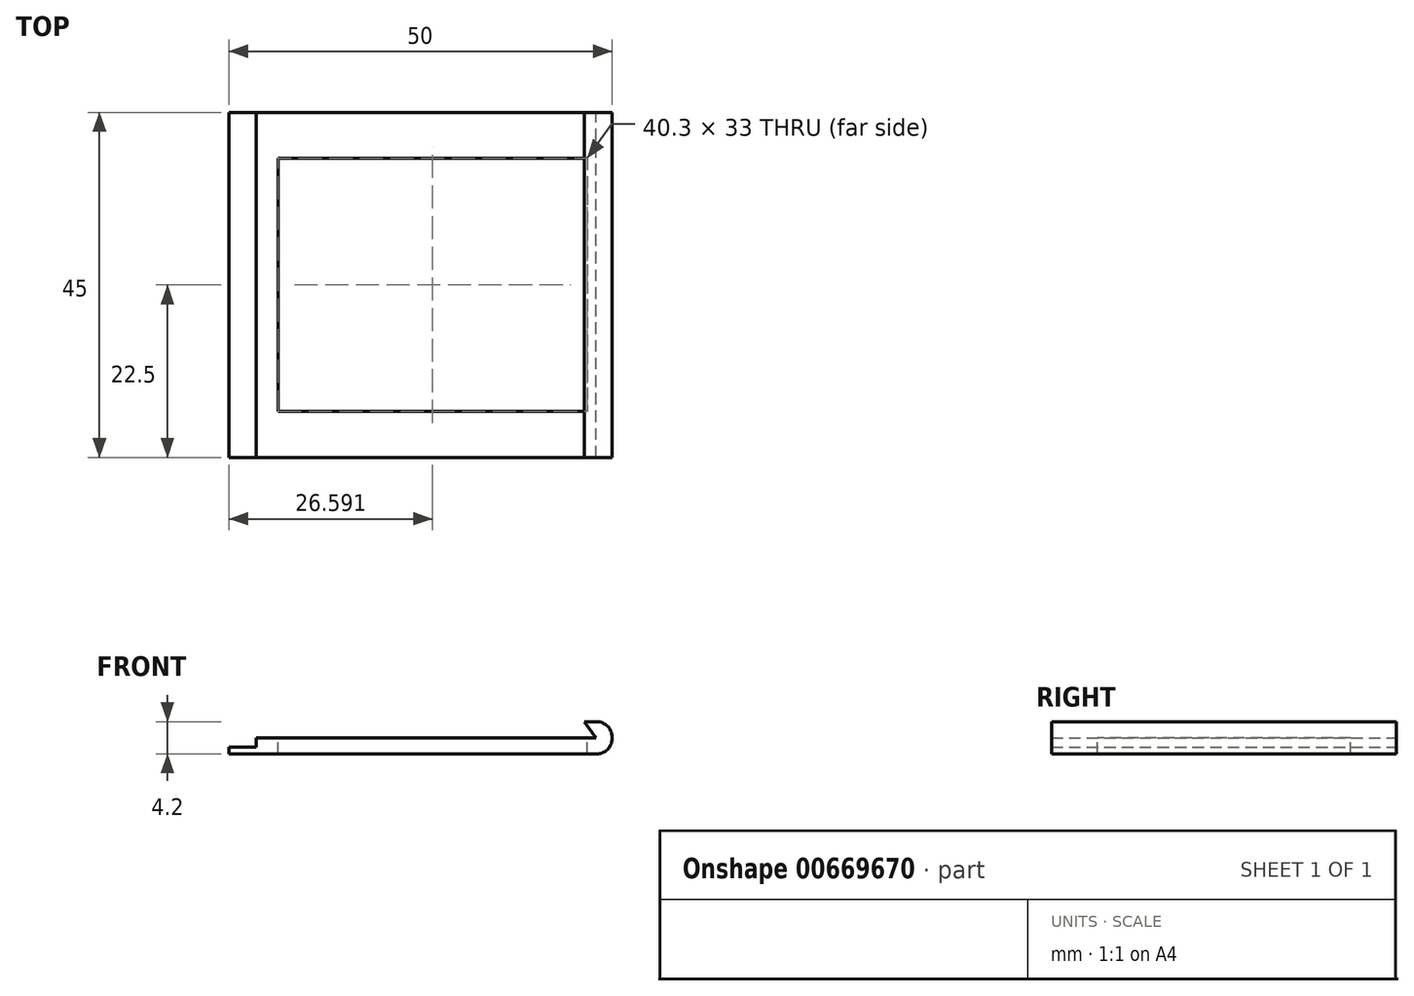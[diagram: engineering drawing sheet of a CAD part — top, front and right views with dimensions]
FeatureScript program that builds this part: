
annotation { "Feature Type Name" : "Feature", "Feature Type Description" : "" }
export const myFeature = defineFeature(function(context is Context, id is Id, definition is map)
    precondition{}
    {
        {
            var Q0;
            Q0=qCreatedBy(makeId("Front.planeOp"),FACE);
            var sketch = newSketch(context, id + "F0", { "sketchPlane" : qUnion([Q0])});
            skLineSegment(sketch, "E0", {"start": v(-9.9, 0.9) * mm, "end": v(-9.9, 0) * mm});
            skLineSegment(sketch, "E1", {"start": v(-9.9, 0) * mm, "end": v(40.1, 0) * mm});
            skLineSegment(sketch, "E2", {"start": v(40.1, 0) * mm, "end": v(40.1, 2.1) * mm});
            skLineSegment(sketch, "E3", {"start": v(40.1, 2.1) * mm, "end": v(-6.3, 2.1) * mm});
            skLineSegment(sketch, "E4", {"start": v(-6.3, 2.1) * mm, "end": v(-6.3, 0.9) * mm});
            skLineSegment(sketch, "E5", {"start": v(-6.3, 0.9) * mm, "end": v(-9.9, 0.9) * mm});
            skLineSegment(sketch, "E6", {"start": v(38, 2.1) * mm, "end": v(36.5, 4.2) * mm});
            skLineSegment(sketch, "E7", {"start": v(36.5, 4.2) * mm, "end": v(40.1, 4.2) * mm});
            skLineSegment(sketch, "E8", {"start": v(40.1, 4.2) * mm, "end": v(40.1, 2.1) * mm});
            skSolve(sketch);
        }
        {
            var Q0;
            Q0=makeQuery(id+"F0.imprint","IMPRINT",FACE,{"disambiguationData":[TD([[makeQuery(id+"F0.imprint","IMPRINT",EDGE,{"derivedFrom":sQuery(id+"F0.wireOp",EDGE,"E0")}),1.0]])]});
            var Q1;
            {var subQ2=sQuery(id+"F0.wireOp",EDGE,"E6");Q1=makeQuery(id+"F0.imprint","IMPRINT",FACE,{"disambiguationData":[TD([[makeQuery(id+"F0.imprint","IMPRINT",EDGE,{"derivedFrom":subQ2}),-1.0]])]});}
            extrude(context, id + "F1", {"entities" : qUnion([Q0, Q1]), "depth" : 45 * mm, "offsetDistance" : 25 * mm});
        }
        {
            var Q0;
            Q0=makeQuery(id+"F1.opExtrude","SWEPT_EDGE",EDGE,{"disambiguationData":[OSD([sQuery(id+"F0.wireOp",EDGE,"E7"),sQuery(id+"F0.wireOp",EDGE,"E8")])]});
            var Q1;
            Q1=makeQuery(id+"F1.opExtrude","SWEPT_EDGE",EDGE,{"disambiguationData":[OSD([sQuery(id+"F0.wireOp",EDGE,"E1"),sQuery(id+"F0.wireOp",EDGE,"E2")])]});
            fillet(context, id + "F2", {"entities" : qUnion([Q0, Q1]), "radius" : 2 * mm, "tangentPropagation" : true, "allowEdgeOverflow" : false});
        }
        {
            var Q0;
            Q0=makeQuery(id+"F1.opExtrude","SWEPT_FACE",FACE,{"disambiguationData":[OSD([sQuery(id+"F0.wireOp",EDGE,"E3")])]});
            var sketch = newSketch(context, id + "F3", { "sketchPlane" : qUnion([Q0])});
            skLineSegment(sketch, "E9.bottom", {"start": v(36.84, -6) * mm, "end": v(-3.46, -6) * mm});
            skLineSegment(sketch, "E9.top", {"start": v(36.84, -39) * mm, "end": v(-3.46, -39) * mm});
            skLineSegment(sketch, "E9.left", {"start": v(36.84, -6) * mm, "end": v(36.84, -39) * mm});
            skLineSegment(sketch, "E9.right", {"start": v(-3.46, -6) * mm, "end": v(-3.46, -39) * mm});
            skSolve(sketch);
        }
        {
            var Q0;
            Q0=makeQuery(id+"F3.imprint","IMPRINT",FACE,{"disambiguationData":[TD([[makeQuery(id+"F3.imprint","IMPRINT",EDGE,{"derivedFrom":sQuery(id+"F3.wireOp",EDGE,"E9.bottom")}),1.0]])]});
            var Q1;
            Q1=makeQuery(id+"F1.opExtrude","SWEPT_BODY",BODY,{"disambiguationData":[OSD([sQuery(id+"F0.wireOp",EDGE,"E0"),sQuery(id+"F0.wireOp",EDGE,"E1"),sQuery(id+"F0.wireOp",EDGE,"E2"),sQuery(id+"F0.wireOp",EDGE,"E3"),sQuery(id+"F0.wireOp",EDGE,"E4"),sQuery(id+"F0.wireOp",EDGE,"E5"),sQuery(id+"F0.wireOp",EDGE,"E6"),sQuery(id+"F0.wireOp",EDGE,"E7"),sQuery(id+"F0.wireOp",EDGE,"E8")])]});
            extrude(context, id + "F4", {"entities" : qUnion([Q0]), "operationType" : NewBodyOperationType.REMOVE, "oppositeDirection" : true, "depth" : 2.1 * mm, "endBoundEntityBody" : qUnion([Q1]), "offsetDistance" : 25 * mm});
        }
    });
